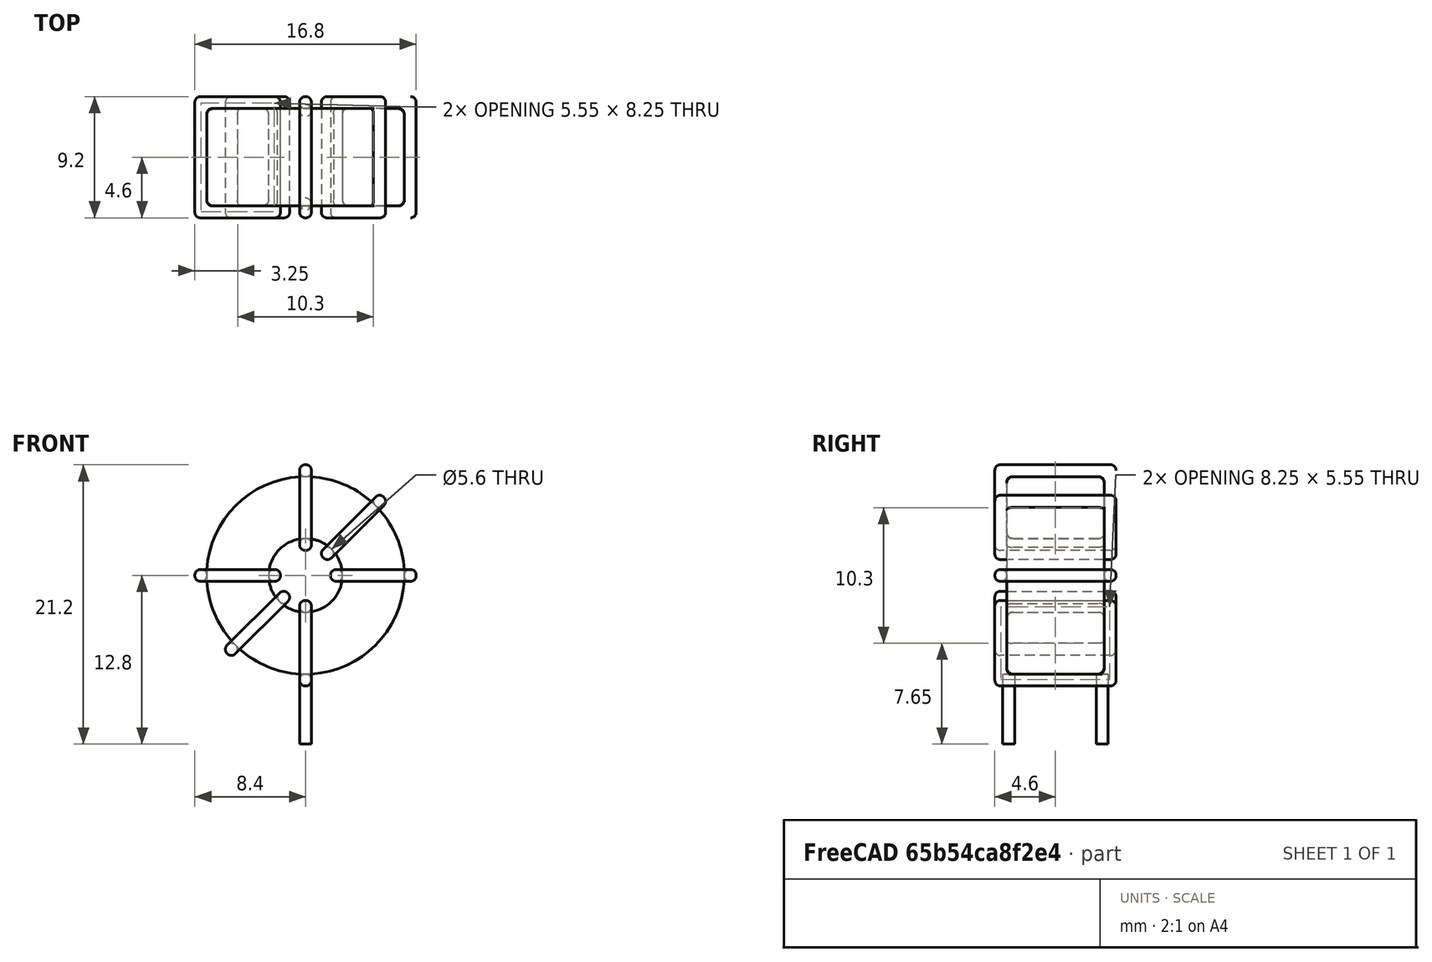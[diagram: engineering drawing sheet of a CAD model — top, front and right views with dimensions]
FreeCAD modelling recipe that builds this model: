
FCSTD DOCUMENT  (FreeCAD 0.16R6703 (Git))
Label: L_Toroid_Vertical_L16.8mm_W9.2mm_P7.10mm_Vishay_TJ3
License: All rights reserved
LicenseURL: http://en.wikipedia.org/wiki/All_rights_reserved
objects: Sketcher::SketchObject×6, PartDesign::Pad×6, PartDesign::Fillet×5, Spreadsheet::Sheet×1
note: 23 computed .brp shape members not serialized (recipe doc carries the construction recipe); baked Part::Feature solids carry a one-line shape summary decoded from their .brp

FEATURE [Spreadsheet::Sheet] Spreadsheet  label="dimensions"
  cells = A1=Wx; B1(Wx)=16.8; C1(WW)=5.600000000000001; D1=16.8; A2=Wy; B2(Wy)=9.199999999999999; D2=9.199999999999999; A3=RM; B3(RMx)=7.1; C3(RMy)=0; A4=d_wire; B4(d_wire)=0.8999999999999999; A5=H; B5(H)=16.8; A6=offsetx; B6(offsetx)=8.4
FEATURE [Sketcher::SketchObject] Sketch
  Placement = pos=(0,-3.55,0) rot=(1,0,0;1.5708rad)
  expr: Placement.Base.y = -Spreadsheet.RMx / 2
  expr: Constraints[0] = Spreadsheet.Wx / 2 - Spreadsheet.d_wire
  expr: Constraints[4] = Spreadsheet.WW / 2
  expr: Constraints[2] = Spreadsheet.Wx / 2 + Spreadsheet.d_wire + 0.5
  sketch-geometry (2):
    g0: Circle CenterX=0 CenterY=9.8 CenterZ=0 NormalX=0 NormalY=0 NormalZ=1 Radius=7.5
    g1: Circle CenterX=0 CenterY=9.8 CenterZ=0 NormalX=0 NormalY=0 NormalZ=1 Radius=2.8
  constraints (5):
    c: Radius(g0) = 7.5
    c: DistanceX(g-1,g0) = 0
    c: DistanceY(g-1,g0) = 9.8
    c: Coincident(g1,g0)
    c: Radius(g1) = 2.8
FEATURE [PartDesign::Pad] Pad
  Length = 7.4
  Length2 = 100
  Midplane = true
  Placement = pos=(0,-3.55,0) rot=(1,0,0;1.5708rad)
  Sketch = -> Sketch
  Type = 0
  expr: Length = Spreadsheet.Wy - 2 * Spreadsheet.d_wire
FEATURE [Sketcher::SketchObject] Sketch001
  Placement = pos=(0,0,1.4) rot=(0,0,1;0rad)
  expr: Placement.Base.z = 0.5 + Spreadsheet.d_wire
  expr: Constraints[4] = Spreadsheet.RMy
  expr: Constraints[2] = -Spreadsheet.RMx
  expr: Constraints[1] = Spreadsheet.d_wire / 2
  sketch-geometry (2):
    g0: Circle CenterX=0 CenterY=0 CenterZ=0 NormalX=0 NormalY=0 NormalZ=1 Radius=0.45
    g1: Circle CenterX=0 CenterY=-7.1 CenterZ=0 NormalX=0 NormalY=0 NormalZ=1 Radius=0.45
  constraints (5):
    c: Equal(g0,g1)
    c: Radius(g0) = 0.45
    c: DistanceY(g-1,g1) = -7.1
    c: Coincident(g0,g-1)
    c: DistanceX(g-1,g1) = 0
FEATURE [PartDesign::Pad] Pad001
  Length = 0.9
  Length2 = 4.4
  Placement = pos=(0,0,1.4) rot=(0,0,1;0rad)
  Reversed = true
  Sketch = -> Sketch001
  Type = 4
  expr: Length2 = 3.5 + Spreadsheet.d_wire
  expr: Length = Spreadsheet.d_wire
FEATURE [PartDesign::Fillet] Fillet
  Base = -> Pad [Edge6,Edge3,Edge2]
  Placement = pos=(0,-3.55,0) rot=(1,0,0;1.5708rad)
  Radius = 0.5
FEATURE [Sketcher::SketchObject] Sketch003
  Placement = pos=(0,1.05,9.8) rot=(1,0,0;3.14159rad)
  expr: Constraints[18] = Spreadsheet.d_wire
  expr: Constraints[16] = Spreadsheet.d_wire
  expr: Constraints[19] = Spreadsheet.d_wire
  expr: Constraints[17] = Spreadsheet.d_wire
  expr: Placement.Base.y = -1 * (Spreadsheet.RMx - Spreadsheet.Wy) / 2
  expr: Constraints[21] = (Spreadsheet.Wx - Spreadsheet.WW) / 2 - Spreadsheet.d_wire
  expr: Constraints[22] = Spreadsheet.Wx / 2 - Spreadsheet.d_wire
  expr: Constraints[43] = Spreadsheet.d_wire
  expr: Constraints[48] = Spreadsheet.Wx - Spreadsheet.d_wire * 2
  expr: Constraints[49] = Spreadsheet.Wy
  expr: Placement.Base.z = Spreadsheet.Wx / 2 + Spreadsheet.d_wire + 0.5
  sketch-geometry (16):
    g0: LineSegment StartX=-1.9 StartY=0 StartZ=0 EndX=-8.4 EndY=0 EndZ=0
    g1: LineSegment StartX=-8.4 StartY=0 StartZ=0 EndX=-8.4 EndY=9.2 EndZ=0
    g2: LineSegment StartX=-8.4 StartY=9.2 StartZ=0 EndX=-1.9 EndY=9.2 EndZ=0
    g3: LineSegment StartX=-1.9 StartY=9.2 StartZ=0 EndX=-1.9 EndY=0 EndZ=0
    g4: LineSegment StartX=-7.5 StartY=8.3 StartZ=0 EndX=-2.8 EndY=8.3 EndZ=0
    g5: LineSegment StartX=-2.8 StartY=8.3 StartZ=0 EndX=-2.8 EndY=0.9 EndZ=0
    g6: LineSegment StartX=-2.8 StartY=0.9 StartZ=0 EndX=-7.5 EndY=0.9 EndZ=0
    g7: LineSegment StartX=-7.5 StartY=0.9 StartZ=0 EndX=-7.5 EndY=8.3 EndZ=0
    g8: LineSegment StartX=1.9 StartY=9.2 StartZ=0 EndX=8.4 EndY=9.2 EndZ=0
    g9: LineSegment StartX=8.4 StartY=9.2 StartZ=0 EndX=8.4 EndY=0 EndZ=0
    g10: LineSegment StartX=8.4 StartY=0 StartZ=0 EndX=1.9 EndY=0 EndZ=0
    g11: LineSegment StartX=1.9 StartY=0 StartZ=0 EndX=1.9 EndY=9.2 EndZ=0
    g12: LineSegment StartX=2.8 StartY=8.3 StartZ=0 EndX=7.5 EndY=8.3 EndZ=0
    g13: LineSegment StartX=7.5 StartY=8.3 StartZ=0 EndX=7.5 EndY=0.9 EndZ=0
    g14: LineSegment StartX=7.5 StartY=0.9 StartZ=0 EndX=2.8 EndY=0.9 EndZ=0
    g15: LineSegment StartX=2.8 StartY=0.9 StartZ=0 EndX=2.8 EndY=8.3 EndZ=0
  constraints (50):
    c: Horizontal(g0)
    c: Coincident(g1,g0)
    c: Vertical(g1)
    c: Coincident(g2,g1)
    c: Horizontal(g2)
    c: Coincident(g3,g2)
    c: Coincident(g3,g0)
    c: Vertical(g3)
    c: Coincident(g4,g5)
    c: Coincident(g5,g6)
    c: Coincident(g6,g7)
    c: Coincident(g7,g4)
    c: Horizontal(g4)
    c: Horizontal(g6)
    c: Vertical(g5)
    c: Vertical(g7)
    c: DistanceX(g1,g4) = 0.9
    c: DistanceY(g4,g1) = 0.9
    c: DistanceX(g5,g0) = 0.9
    c: DistanceY(g0,g5) = 0.9
    c: DistanceY(g-1,g0) = 0
    c: DistanceX(g6,g6) = 4.7
    c: DistanceX(g6,g-1) = 7.5
    c: Coincident(g8,g9)
    c: Coincident(g9,g10)
    c: Coincident(g10,g11)
    c: Coincident(g11,g8)
    c: Horizontal(g8)
    c: Horizontal(g10)
    c: Vertical(g9)
    c: Vertical(g11)
    c: Coincident(g12,g13)
    c: Coincident(g13,g14)
    c: Coincident(g14,g15)
    c: Coincident(g15,g12)
    c: Horizontal(g12)
    c: Horizontal(g14)
    c: Vertical(g13)
    c: Vertical(g15)
    c: DistanceY(g8,g2) = 0
    c: DistanceY(g10,g0) = 0
    c: DistanceY(g14,g5) = 0
    c: DistanceY(g12,g4) = 0
    c: DistanceX(g8,g12) = 0.9
    c: Equal(g8,g2)
    c: Equal(g12,g4)
    c: Equal(g9,g1)
    c: Equal(g13,g7)
    c: DistanceX(g4,g12) = 15
    c: DistanceY(g0,g1) = 9.2
FEATURE [PartDesign::Pad] Pad002
  Length = 0.9
  Length2 = 100
  Midplane = true
  Placement = pos=(0,1.05,9.8) rot=(1,0,0;3.14159rad)
  Sketch = -> Sketch003
  Type = 0
  expr: Length = Spreadsheet.d_wire
FEATURE [PartDesign::Fillet] Fillet001
  Base = -> Pad002 [Edge38,Edge41,Edge42,Edge43,Edge29,Edge32,Edge33,Edge34,Edge25,Edge35,Edge36,Edge13,Edge14,Edge15,Edge16,Edge17,Edge18,Edge19,Edge1,Edge2,Edge3,Edge4,Edge5,Edge6,Edge7,Edge37,Edge39,Edge40,Edge20,Edge23,Edge24,Edge21,Edge22,Edge8,Edge9,Edge10,Edge11,Edge12,Edge26,Edge27,+8 more]
  Placement = pos=(0,1.05,9.8) rot=(1,0,0;3.14159rad)
  Radius = 0.423
  expr: Radius = Spreadsheet.d_wire * 0.47
FEATURE [Sketcher::SketchObject] Sketch004
  Placement = pos=(0,1.05,9.8) rot=(0.92388,0,0.382683;3.14159rad)
  expr: Constraints[18] = Spreadsheet.d_wire
  expr: Constraints[16] = Spreadsheet.d_wire
  expr: Constraints[19] = Spreadsheet.d_wire
  expr: Constraints[17] = Spreadsheet.d_wire
  expr: Placement.Base.y = -1 * (Spreadsheet.RMx - Spreadsheet.Wy) / 2
  expr: Constraints[21] = (Spreadsheet.Wx - Spreadsheet.WW) / 2 - Spreadsheet.d_wire
  expr: Constraints[22] = Spreadsheet.Wx / 2 - Spreadsheet.d_wire
  expr: Constraints[43] = Spreadsheet.d_wire
  expr: Constraints[48] = Spreadsheet.Wx - 2 * Spreadsheet.d_wire
  expr: Constraints[49] = Spreadsheet.Wy
  expr: Placement.Base.z = Spreadsheet.Wx / 2 + Spreadsheet.d_wire + 0.5
  sketch-geometry (16):
    g0: LineSegment StartX=-1.9 StartY=0 StartZ=0 EndX=-8.4 EndY=0 EndZ=0
    g1: LineSegment StartX=-8.4 StartY=0 StartZ=0 EndX=-8.4 EndY=9.2 EndZ=0
    g2: LineSegment StartX=-8.4 StartY=9.2 StartZ=0 EndX=-1.9 EndY=9.2 EndZ=0
    g3: LineSegment StartX=-1.9 StartY=9.2 StartZ=0 EndX=-1.9 EndY=0 EndZ=0
    g4: LineSegment StartX=-7.5 StartY=8.3 StartZ=0 EndX=-2.8 EndY=8.3 EndZ=0
    g5: LineSegment StartX=-2.8 StartY=8.3 StartZ=0 EndX=-2.8 EndY=0.9 EndZ=0
    g6: LineSegment StartX=-2.8 StartY=0.9 StartZ=0 EndX=-7.5 EndY=0.9 EndZ=0
    g7: LineSegment StartX=-7.5 StartY=0.9 StartZ=0 EndX=-7.5 EndY=8.3 EndZ=0
    g8: LineSegment StartX=1.9 StartY=9.2 StartZ=0 EndX=8.4 EndY=9.2 EndZ=0
    g9: LineSegment StartX=8.4 StartY=9.2 StartZ=0 EndX=8.4 EndY=0 EndZ=0
    g10: LineSegment StartX=8.4 StartY=0 StartZ=0 EndX=1.9 EndY=0 EndZ=0
    g11: LineSegment StartX=1.9 StartY=0 StartZ=0 EndX=1.9 EndY=9.2 EndZ=0
    g12: LineSegment StartX=2.8 StartY=8.3 StartZ=0 EndX=7.5 EndY=8.3 EndZ=0
    g13: LineSegment StartX=7.5 StartY=8.3 StartZ=0 EndX=7.5 EndY=0.9 EndZ=0
    g14: LineSegment StartX=7.5 StartY=0.9 StartZ=0 EndX=2.8 EndY=0.9 EndZ=0
    g15: LineSegment StartX=2.8 StartY=0.9 StartZ=0 EndX=2.8 EndY=8.3 EndZ=0
  constraints (50):
    c: Horizontal(g0)
    c: Coincident(g1,g0)
    c: Vertical(g1)
    c: Coincident(g2,g1)
    c: Horizontal(g2)
    c: Coincident(g3,g2)
    c: Coincident(g3,g0)
    c: Vertical(g3)
    c: Coincident(g4,g5)
    c: Coincident(g5,g6)
    c: Coincident(g6,g7)
    c: Coincident(g7,g4)
    c: Horizontal(g4)
    c: Horizontal(g6)
    c: Vertical(g5)
    c: Vertical(g7)
    c: DistanceX(g1,g4) = 0.9
    c: DistanceY(g4,g1) = 0.9
    c: DistanceX(g5,g0) = 0.9
    c: DistanceY(g0,g5) = 0.9
    c: DistanceY(g-1,g0) = 0
    c: DistanceX(g6,g6) = 4.7
    c: DistanceX(g6,g-1) = 7.5
    c: Coincident(g8,g9)
    c: Coincident(g9,g10)
    c: Coincident(g10,g11)
    c: Coincident(g11,g8)
    c: Horizontal(g8)
    c: Horizontal(g10)
    c: Vertical(g9)
    c: Vertical(g11)
    c: Coincident(g12,g13)
    c: Coincident(g13,g14)
    c: Coincident(g14,g15)
    c: Coincident(g15,g12)
    c: Horizontal(g12)
    c: Horizontal(g14)
    c: Vertical(g13)
    c: Vertical(g15)
    c: DistanceY(g8,g2) = 0
    c: DistanceY(g10,g0) = 0
    c: DistanceY(g14,g5) = 0
    c: DistanceY(g12,g4) = 0
    c: DistanceX(g8,g12) = 0.9
    c: Equal(g8,g2)
    c: Equal(g12,g4)
    c: Equal(g9,g1)
    c: Equal(g13,g7)
    c: DistanceX(g4,g12) = 15
    c: DistanceY(g0,g1) = 9.2
FEATURE [PartDesign::Pad] Pad003
  Length = 0.9
  Length2 = 100
  Midplane = true
  Placement = pos=(0,1.05,9.8) rot=(0.92388,0,0.382683;3.14159rad)
  Sketch = -> Sketch004
  Type = 0
  expr: Length = Spreadsheet.d_wire
FEATURE [PartDesign::Fillet] Fillet002
  Base = -> Pad003 [Edge38,Edge41,Edge42,Edge43,Edge29,Edge32,Edge33,Edge34,Edge25,Edge35,Edge36,Edge13,Edge14,Edge15,Edge16,Edge17,Edge18,Edge19,Edge1,Edge2,Edge3,Edge4,Edge5,Edge6,Edge7,Edge37,Edge39,Edge40,Edge20,Edge23,Edge24,Edge21,Edge22,Edge8,Edge9,Edge10,Edge11,Edge12,Edge26,Edge27,+8 more]
  Placement = pos=(0,1.05,9.8) rot=(0.92388,0,0.382683;3.14159rad)
  Radius = 0.423
  expr: Radius = Spreadsheet.d_wire * 0.47
FEATURE [Sketcher::SketchObject] Sketch005
  Placement = pos=(0,1.05,9.8) rot=(0.92388,0,-0.382683;3.14159rad)
  expr: Constraints[18] = Spreadsheet.d_wire
  expr: Constraints[16] = Spreadsheet.d_wire
  expr: Constraints[19] = Spreadsheet.d_wire
  expr: Constraints[17] = Spreadsheet.d_wire
  expr: Placement.Base.y = -1 * (Spreadsheet.RMx - Spreadsheet.Wy) / 2
  expr: Constraints[21] = (Spreadsheet.Wx - Spreadsheet.WW) / 2 - Spreadsheet.d_wire
  expr: Constraints[22] = Spreadsheet.Wx / 2 - Spreadsheet.d_wire
  expr: Constraints[43] = Spreadsheet.d_wire
  expr: Constraints[48] = Spreadsheet.Wx - 2 * Spreadsheet.d_wire
  expr: Constraints[49] = Spreadsheet.Wy
  expr: Placement.Base.z = Spreadsheet.Wx / 2 + Spreadsheet.d_wire + 0.5
  sketch-geometry (16):
    g0: LineSegment StartX=-1.9 StartY=0 StartZ=0 EndX=-8.4 EndY=0 EndZ=0
    g1: LineSegment StartX=-8.4 StartY=0 StartZ=0 EndX=-8.4 EndY=9.2 EndZ=0
    g2: LineSegment StartX=-8.4 StartY=9.2 StartZ=0 EndX=-1.9 EndY=9.2 EndZ=0
    g3: LineSegment StartX=-1.9 StartY=9.2 StartZ=0 EndX=-1.9 EndY=0 EndZ=0
    g4: LineSegment StartX=-7.5 StartY=8.3 StartZ=0 EndX=-2.8 EndY=8.3 EndZ=0
    g5: LineSegment StartX=-2.8 StartY=8.3 StartZ=0 EndX=-2.8 EndY=0.9 EndZ=0
    g6: LineSegment StartX=-2.8 StartY=0.9 StartZ=0 EndX=-7.5 EndY=0.9 EndZ=0
    g7: LineSegment StartX=-7.5 StartY=0.9 StartZ=0 EndX=-7.5 EndY=8.3 EndZ=0
    g8: LineSegment StartX=1.9 StartY=9.2 StartZ=0 EndX=8.4 EndY=9.2 EndZ=0
    g9: LineSegment StartX=8.4 StartY=9.2 StartZ=0 EndX=8.4 EndY=0 EndZ=0
    g10: LineSegment StartX=8.4 StartY=0 StartZ=0 EndX=1.9 EndY=0 EndZ=0
    g11: LineSegment StartX=1.9 StartY=0 StartZ=0 EndX=1.9 EndY=9.2 EndZ=0
    g12: LineSegment StartX=2.8 StartY=8.3 StartZ=0 EndX=7.5 EndY=8.3 EndZ=0
    g13: LineSegment StartX=7.5 StartY=8.3 StartZ=0 EndX=7.5 EndY=0.9 EndZ=0
    g14: LineSegment StartX=7.5 StartY=0.9 StartZ=0 EndX=2.8 EndY=0.9 EndZ=0
    g15: LineSegment StartX=2.8 StartY=0.9 StartZ=0 EndX=2.8 EndY=8.3 EndZ=0
  constraints (50):
    c: Horizontal(g0)
    c: Coincident(g1,g0)
    c: Vertical(g1)
    c: Coincident(g2,g1)
    c: Horizontal(g2)
    c: Coincident(g3,g2)
    c: Coincident(g3,g0)
    c: Vertical(g3)
    c: Coincident(g4,g5)
    c: Coincident(g5,g6)
    c: Coincident(g6,g7)
    c: Coincident(g7,g4)
    c: Horizontal(g4)
    c: Horizontal(g6)
    c: Vertical(g5)
    c: Vertical(g7)
    c: DistanceX(g1,g4) = 0.9
    c: DistanceY(g4,g1) = 0.9
    c: DistanceX(g5,g0) = 0.9
    c: DistanceY(g0,g5) = 0.9
    c: DistanceY(g-1,g0) = 0
    c: DistanceX(g6,g6) = 4.7
    c: DistanceX(g6,g-1) = 7.5
    c: Coincident(g8,g9)
    c: Coincident(g9,g10)
    c: Coincident(g10,g11)
    c: Coincident(g11,g8)
    c: Horizontal(g8)
    c: Horizontal(g10)
    c: Vertical(g9)
    c: Vertical(g11)
    c: Coincident(g12,g13)
    c: Coincident(g13,g14)
    c: Coincident(g14,g15)
    c: Coincident(g15,g12)
    c: Horizontal(g12)
    c: Horizontal(g14)
    c: Vertical(g13)
    c: Vertical(g15)
    c: DistanceY(g8,g2) = 0
    c: DistanceY(g10,g0) = 0
    c: DistanceY(g14,g5) = 0
    c: DistanceY(g12,g4) = 0
    c: DistanceX(g8,g12) = 0.9
    c: Equal(g8,g2)
    c: Equal(g12,g4)
    c: Equal(g9,g1)
    c: Equal(g13,g7)
    c: DistanceX(g4,g12) = 15
    c: DistanceY(g0,g1) = 9.2
FEATURE [PartDesign::Pad] Pad004
  Length = 0.9
  Length2 = 100
  Midplane = true
  Placement = pos=(0,1.05,9.8) rot=(0.92388,0,-0.382683;3.14159rad)
  Sketch = -> Sketch005
  Type = 0
  expr: Length = Spreadsheet.d_wire
FEATURE [PartDesign::Fillet] Fillet003
  Base = -> Pad004 [Edge38,Edge41,Edge42,Edge43,Edge29,Edge32,Edge33,Edge34,Edge25,Edge35,Edge36,Edge13,Edge14,Edge15,Edge16,Edge17,Edge18,Edge19,Edge1,Edge2,Edge3,Edge4,Edge5,Edge6,Edge7,Edge37,Edge39,Edge40,Edge20,Edge23,Edge24,Edge21,Edge22,Edge8,Edge9,Edge10,Edge11,Edge12,Edge26,Edge27,+8 more]
  Placement = pos=(0,1.05,9.8) rot=(0.92388,0,-0.382683;3.14159rad)
  Radius = 0.423
  expr: Radius = Spreadsheet.d_wire * 0.47
FEATURE [Sketcher::SketchObject] Sketch006
  Placement = pos=(0,1.05,9.8) rot=(0.707107,0,0.707107;3.14159rad)
  expr: Constraints[18] = Spreadsheet.d_wire
  expr: Constraints[16] = Spreadsheet.d_wire
  expr: Constraints[19] = Spreadsheet.d_wire
  expr: Constraints[17] = Spreadsheet.d_wire
  expr: Placement.Base.y = -1 * (Spreadsheet.RMx - Spreadsheet.Wy) / 2
  expr: Constraints[21] = (Spreadsheet.Wx - Spreadsheet.WW) / 2 - Spreadsheet.d_wire
  expr: Constraints[22] = Spreadsheet.Wx / 2 - Spreadsheet.d_wire
  expr: Constraints[43] = Spreadsheet.d_wire
  expr: Constraints[48] = Spreadsheet.Wx - Spreadsheet.d_wire * 2
  expr: Constraints[49] = Spreadsheet.Wy
  expr: Placement.Base.z = Spreadsheet.Wx / 2 + Spreadsheet.d_wire + 0.5
  sketch-geometry (16):
    g0: LineSegment StartX=-1.9 StartY=0 StartZ=0 EndX=-8.4 EndY=0 EndZ=0
    g1: LineSegment StartX=-8.4 StartY=0 StartZ=0 EndX=-8.4 EndY=9.2 EndZ=0
    g2: LineSegment StartX=-8.4 StartY=9.2 StartZ=0 EndX=-1.9 EndY=9.2 EndZ=0
    g3: LineSegment StartX=-1.9 StartY=9.2 StartZ=0 EndX=-1.9 EndY=0 EndZ=0
    g4: LineSegment StartX=-7.5 StartY=8.3 StartZ=0 EndX=-2.8 EndY=8.3 EndZ=0
    g5: LineSegment StartX=-2.8 StartY=8.3 StartZ=0 EndX=-2.8 EndY=0.9 EndZ=0
    g6: LineSegment StartX=-2.8 StartY=0.9 StartZ=0 EndX=-7.5 EndY=0.9 EndZ=0
    g7: LineSegment StartX=-7.5 StartY=0.9 StartZ=0 EndX=-7.5 EndY=8.3 EndZ=0
    g8: LineSegment StartX=1.9 StartY=9.2 StartZ=0 EndX=8.4 EndY=9.2 EndZ=0
    g9: LineSegment StartX=8.4 StartY=9.2 StartZ=0 EndX=8.4 EndY=0 EndZ=0
    g10: LineSegment StartX=8.4 StartY=0 StartZ=0 EndX=1.9 EndY=0 EndZ=0
    g11: LineSegment StartX=1.9 StartY=0 StartZ=0 EndX=1.9 EndY=9.2 EndZ=0
    g12: LineSegment StartX=2.8 StartY=8.3 StartZ=0 EndX=7.5 EndY=8.3 EndZ=0
    g13: LineSegment StartX=7.5 StartY=8.3 StartZ=0 EndX=7.5 EndY=0.9 EndZ=0
    g14: LineSegment StartX=7.5 StartY=0.9 StartZ=0 EndX=2.8 EndY=0.9 EndZ=0
    g15: LineSegment StartX=2.8 StartY=0.9 StartZ=0 EndX=2.8 EndY=8.3 EndZ=0
  constraints (50):
    c: Horizontal(g0)
    c: Coincident(g1,g0)
    c: Vertical(g1)
    c: Coincident(g2,g1)
    c: Horizontal(g2)
    c: Coincident(g3,g2)
    c: Coincident(g3,g0)
    c: Vertical(g3)
    c: Coincident(g4,g5)
    c: Coincident(g5,g6)
    c: Coincident(g6,g7)
    c: Coincident(g7,g4)
    c: Horizontal(g4)
    c: Horizontal(g6)
    c: Vertical(g5)
    c: Vertical(g7)
    c: DistanceX(g1,g4) = 0.9
    c: DistanceY(g4,g1) = 0.9
    c: DistanceX(g5,g0) = 0.9
    c: DistanceY(g0,g5) = 0.9
    c: DistanceY(g-1,g0) = 0
    c: DistanceX(g6,g6) = 4.7
    c: DistanceX(g6,g-1) = 7.5
    c: Coincident(g8,g9)
    c: Coincident(g9,g10)
    c: Coincident(g10,g11)
    c: Coincident(g11,g8)
    c: Horizontal(g8)
    c: Horizontal(g10)
    c: Vertical(g9)
    c: Vertical(g11)
    c: Coincident(g12,g13)
    c: Coincident(g13,g14)
    c: Coincident(g14,g15)
    c: Coincident(g15,g12)
    c: Horizontal(g12)
    c: Horizontal(g14)
    c: Vertical(g13)
    c: Vertical(g15)
    c: DistanceY(g8,g2) = 0
    c: DistanceY(g10,g0) = 0
    c: DistanceY(g14,g5) = 0
    c: DistanceY(g12,g4) = 0
    c: DistanceX(g8,g12) = 0.9
    c: Equal(g8,g2)
    c: Equal(g12,g4)
    c: Equal(g9,g1)
    c: Equal(g13,g7)
    c: DistanceX(g4,g12) = 15
    c: DistanceY(g0,g1) = 9.2
FEATURE [PartDesign::Pad] Pad005
  Length = 0.9
  Length2 = 100
  Midplane = true
  Placement = pos=(0,1.05,9.8) rot=(0.707107,0,0.707107;3.14159rad)
  Sketch = -> Sketch006
  Type = 0
  expr: Length = Spreadsheet.d_wire
FEATURE [PartDesign::Fillet] Fillet004
  Base = -> Pad005 [Edge38,Edge41,Edge42,Edge43,Edge29,Edge32,Edge33,Edge34,Edge25,Edge35,Edge36,Edge13,Edge14,Edge15,Edge16,Edge17,Edge18,Edge19,Edge1,Edge2,Edge3,Edge4,Edge5,Edge6,Edge7,Edge37,Edge39,Edge40,Edge20,Edge23,Edge24,Edge21,Edge22,Edge8,Edge9,Edge10,Edge11,Edge12,Edge26,Edge27,+8 more]
  Placement = pos=(0,1.05,9.8) rot=(0.707107,0,0.707107;3.14159rad)
  Radius = 0.423
  expr: Radius = Spreadsheet.d_wire * 0.47
